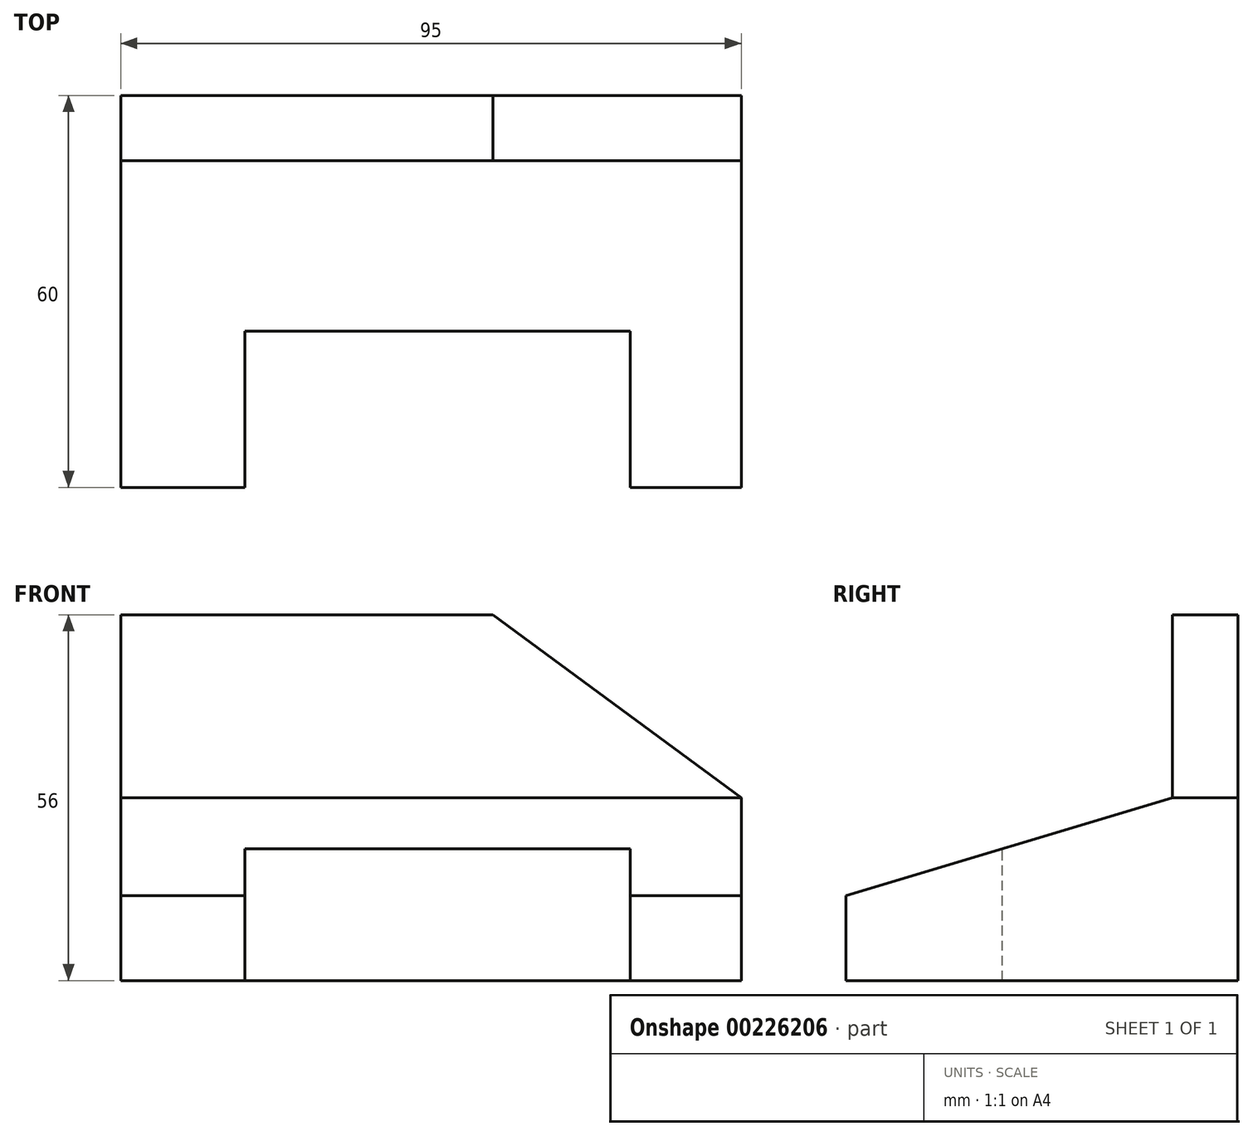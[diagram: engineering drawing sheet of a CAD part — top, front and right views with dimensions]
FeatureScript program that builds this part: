
annotation { "Feature Type Name" : "Feature", "Feature Type Description" : "" }
export const myFeature = defineFeature(function(context is Context, id is Id, definition is map)
    precondition{}
    {
        {
            var Q0;
            Q0=qCreatedBy(makeId("Right.planeOp"),FACE);
            var sketch = newSketch(context, id + "F0", { "sketchPlane" : qUnion([Q0])});
            skLineSegment(sketch, "E0", {"start": v(-29.44, -42.42) * mm, "end": v(30.56, -42.42) * mm});
            skLineSegment(sketch, "E1", {"start": v(30.56, 13.58) * mm, "end": v(30.56, -42.42) * mm});
            skLineSegment(sketch, "E2", {"start": v(30.56, 13.58) * mm, "end": v(20.56, 13.58) * mm});
            skLineSegment(sketch, "E3", {"start": v(20.56, 13.58) * mm, "end": v(20.56, -14.42) * mm});
            skLineSegment(sketch, "E4", {"start": v(20.56, -14.42) * mm, "end": v(-29.44, -29.42) * mm});
            skLineSegment(sketch, "E5", {"start": v(-29.44, -29.42) * mm, "end": v(-29.44, -42.42) * mm});
            skLineSegment(sketch, "E6", {"start": v(20.56, -14.42) * mm, "end": v(30.56, -14.42) * mm});
            skSolve(sketch);
        }
        {
            var Q0;
            {var subQ0=sQuery(id+"F0.wireOp",EDGE,"E2");Q0=makeQuery(id+"F0.imprint","IMPRINT",FACE,{"disambiguationData":[TD([[makeQuery(id+"F0.imprint","IMPRINT",EDGE,{"derivedFrom":subQ0}),1.0]])]});}
            var Q1;
            {var subQ1=sQuery(id+"F0.wireOp",EDGE,"E0");Q1=makeQuery(id+"F0.imprint","IMPRINT",FACE,{"disambiguationData":[TD([[makeQuery(id+"F0.imprint","IMPRINT",EDGE,{"derivedFrom":subQ1}),1.0]])]});}
            extrude(context, id + "F1", {"entities" : qUnion([Q0, Q1]), "depth" : 95 * mm});
        }
        {
            var Q0;
            Q0=makeQuery(id+"F1.opExtrude","SWEPT_FACE",FACE,{"disambiguationData":[OSD([sQuery(id+"F0.wireOp",EDGE,"E3")])]});
            var sketch = newSketch(context, id + "F2", { "sketchPlane" : qUnion([Q0])});
            skLineSegment(sketch, "E7", {"start": v(0, 13.58) * mm, "end": v(57, 13.58) * mm});
            skLineSegment(sketch, "E8", {"start": v(57, 13.58) * mm, "end": v(95, -14.42) * mm});
            skLineSegment(sketch, "E9", {"start": v(57, 13.58) * mm, "end": v(95, 13.58) * mm});
            skLineSegment(sketch, "E10", {"start": v(95, 13.58) * mm, "end": v(95, -14.42) * mm});
            skSolve(sketch);
        }
        {
            var Q0;
            Q0=makeQuery(id+"F2.imprint","IMPRINT",FACE,{"disambiguationData":[TD([[makeQuery(id+"F2.imprint","IMPRINT",EDGE,{"derivedFrom":sQuery(id+"F2.wireOp",EDGE,"E8")}),1.0]])]});
            extrude(context, id + "F3", {"entities" : qUnion([Q0]), "operationType" : NewBodyOperationType.REMOVE, "oppositeDirection" : true, "depth" : 39.5 * mm});
        }
        {
            var Q0;
            Q0=qCreatedBy(makeId("Top.planeOp"),FACE);
            var sketch = newSketch(context, id + "F4", { "sketchPlane" : qUnion([Q0])});
            skLineSegment(sketch, "E11", {"start": v(0, -29.5) * mm, "end": v(19, -29.5) * mm});
            skLineSegment(sketch, "E12", {"start": v(19, -29.5) * mm, "end": v(19, -5.5) * mm});
            skLineSegment(sketch, "E13", {"start": v(19, -5.5) * mm, "end": v(78, -5.5) * mm});
            skLineSegment(sketch, "E14", {"start": v(78, -5.5) * mm, "end": v(78, -29.5) * mm});
            skLineSegment(sketch, "E15", {"start": v(78, -29.5) * mm, "end": v(19, -29.5) * mm});
            skSolve(sketch);
        }
        {
            var Q0;
            Q0=makeQuery(id+"F4.imprint","IMPRINT",FACE,{"disambiguationData":[TD([[makeQuery(id+"F4.imprint","IMPRINT",EDGE,{"derivedFrom":sQuery(id+"F4.wireOp",EDGE,"E12")}),-1.0]])]});
            extrude(context, id + "F5", {"entities" : qUnion([Q0]), "operationType" : NewBodyOperationType.REMOVE, "oppositeDirection" : true, "depth" : 192 * mm});
        }
    });
